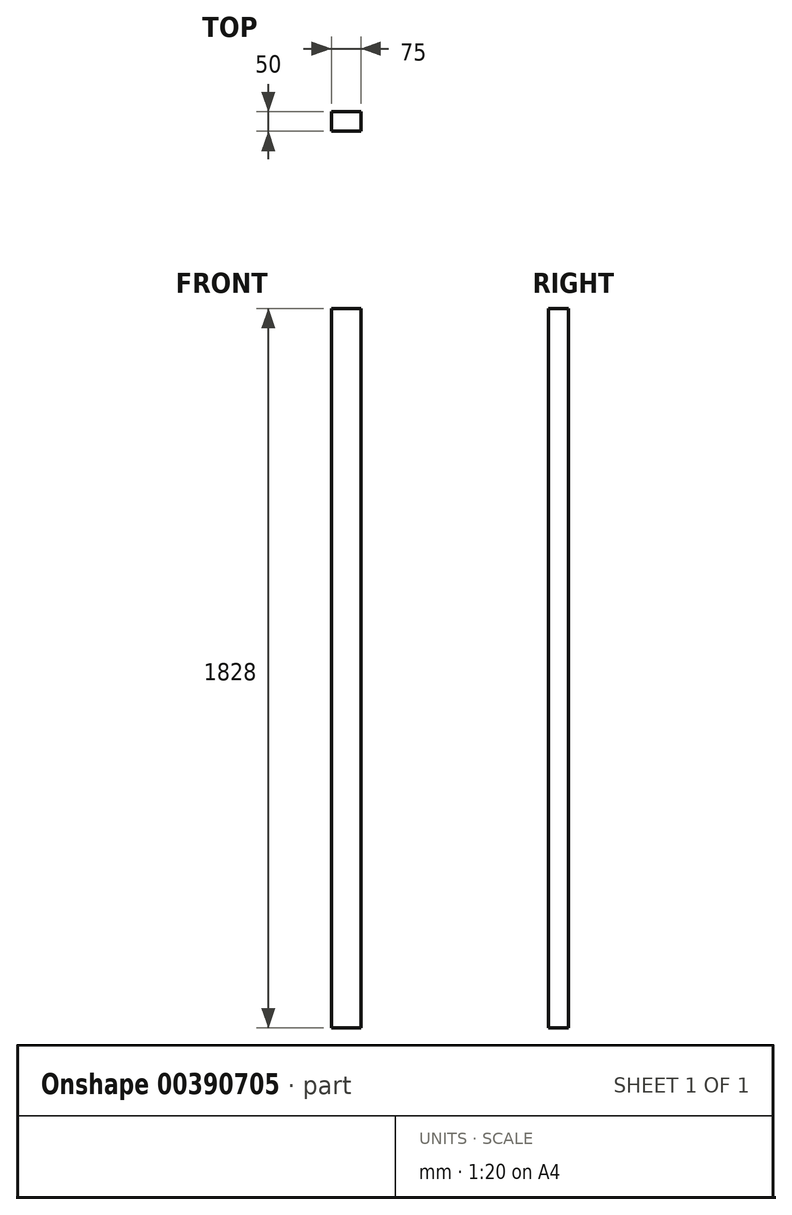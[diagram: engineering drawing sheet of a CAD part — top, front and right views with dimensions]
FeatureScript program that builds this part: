
annotation { "Feature Type Name" : "Feature", "Feature Type Description" : "" }
export const myFeature = defineFeature(function(context is Context, id is Id, definition is map)
    precondition{}
    {
        {
            var Q0;
            Q0=qCreatedBy(makeId("Top.planeOp"),FACE);
            var sketch = newSketch(context, id + "F0", { "sketchPlane" : qUnion([Q0])});
            skLineSegment(sketch, "E0.bottom", {"start": v(0, 0) * mm, "end": v(75, 0) * mm});
            skLineSegment(sketch, "E0.top", {"start": v(0, 50) * mm, "end": v(75, 50) * mm});
            skLineSegment(sketch, "E0.left", {"start": v(0, 0) * mm, "end": v(0, 50) * mm});
            skLineSegment(sketch, "E0.right", {"start": v(75, 0) * mm, "end": v(75, 50) * mm});
            skSolve(sketch);
        }
        {
            var Q0;
            Q0 = qSketchRegion(id + "F0", true);
            extrude(context, id + "F1", {"entities" : qUnion([Q0]), "depth" : 1828 * mm});
        }
    });
